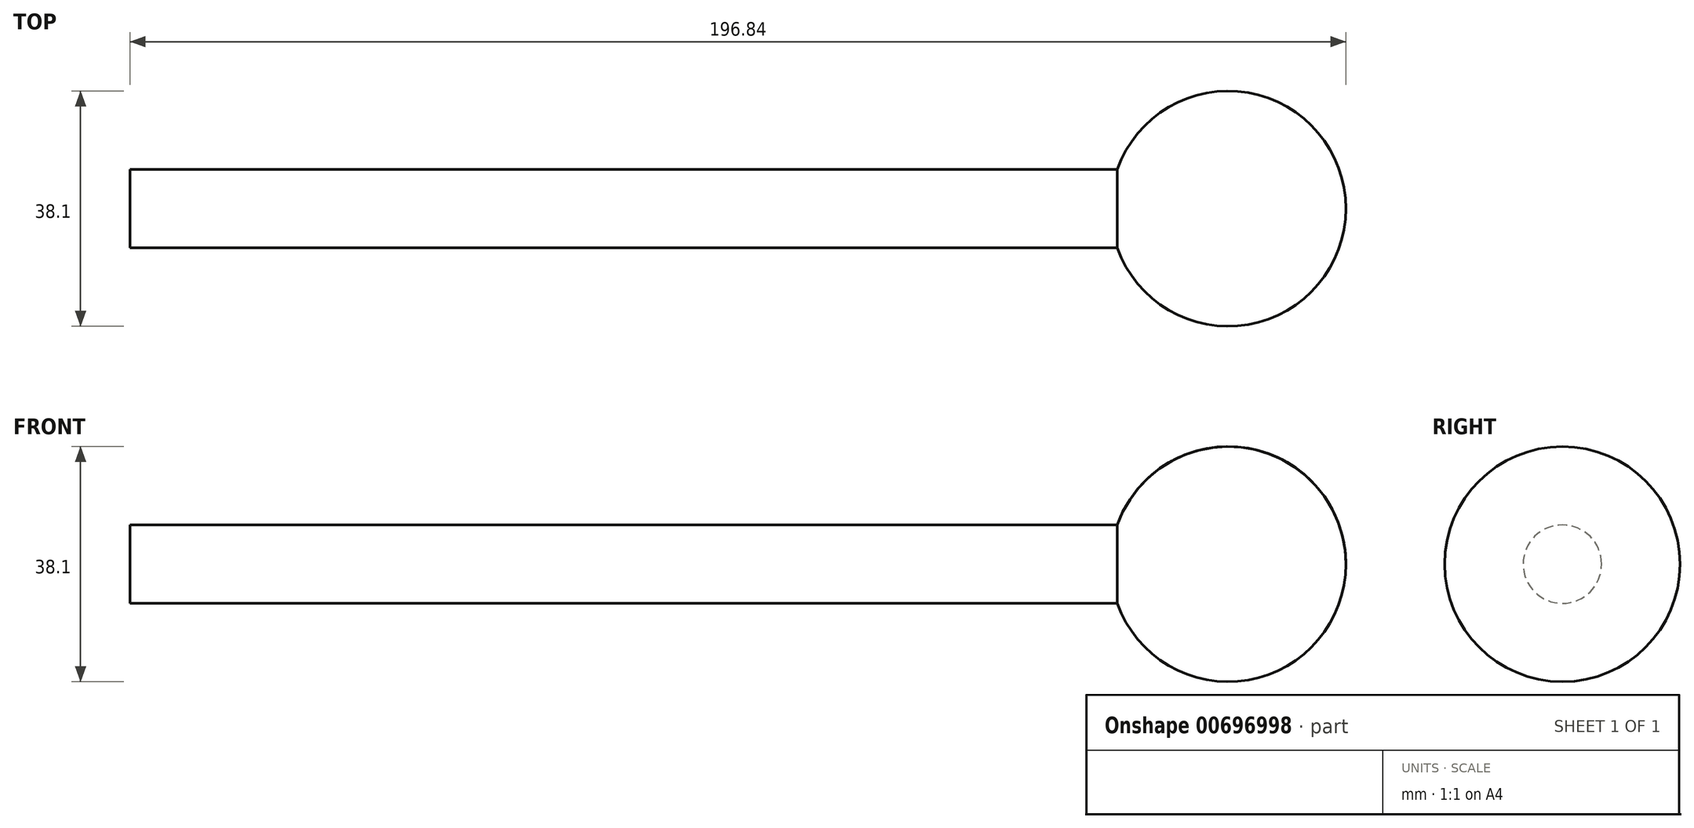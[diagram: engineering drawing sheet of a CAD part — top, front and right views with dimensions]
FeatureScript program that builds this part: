
annotation { "Feature Type Name" : "Feature", "Feature Type Description" : "" }
export const myFeature = defineFeature(function(context is Context, id is Id, definition is map)
    precondition{}
    {
        {
            var Q0;
            Q0=qCreatedBy(makeId("Front.planeOp"),FACE);
            var sketch = newSketch(context, id + "F0", { "sketchPlane" : qUnion([Q0])});
            skLineSegment(sketch, "E0", {"start": v(0, 0) * mm, "end": v(196.84, 0) * mm});
            skLineSegment(sketch, "E1", {"start": v(0, 0) * mm, "end": v(0, 6.35) * mm});
            skLineSegment(sketch, "E2", {"start": v(0, 6.35) * mm, "end": v(159.83, 6.35) * mm});
            skArc(sketch, "E3", {"start": v(196.84, 0) * mm, "mid": v(177.79, 19.05) * mm, "end": v(158.74, 0) * mm});
            skSolve(sketch);
        }
        {
            var Q0;
            {var subQ0=sQuery(id+"F0.wireOp",EDGE,"E3");var subQ1=sQuery(id+"F0.wireOp",EDGE,"E0");var subQ2=makeQuery(id+"F0.imprint","INTERSECT",VERTEX,{"disambiguationData":[OD(0.0)],"derivedFrom":[subQ1,subQ0]});Q0=makeQuery(id+"F0.imprint","IMPRINT",FACE,{"disambiguationData":[TD([[makeQuery(id+"F0.imprint","IMPRINT",EDGE,{"disambiguationData":[TD([[subQ2,1.0]])],"derivedFrom":subQ1}),1.0]])]});}
            var Q1;
            {var subQ0=sQuery(id+"F0.wireOp",EDGE,"E1");Q1=makeQuery(id+"F0.imprint","IMPRINT",FACE,{"disambiguationData":[TD([[makeQuery(id+"F0.imprint","IMPRINT",EDGE,{"derivedFrom":subQ0}),-1.0]])]});}
            var Q2;
            Q2=sQuery(id+"F0.wireOp",EDGE,"E0");
            revolve(context, id + "F1", {"entities" : qUnion([Q0, Q1]), "axis" : qUnion([Q2]), "revolveType" : RevolveType.FULL});
        }
    });
